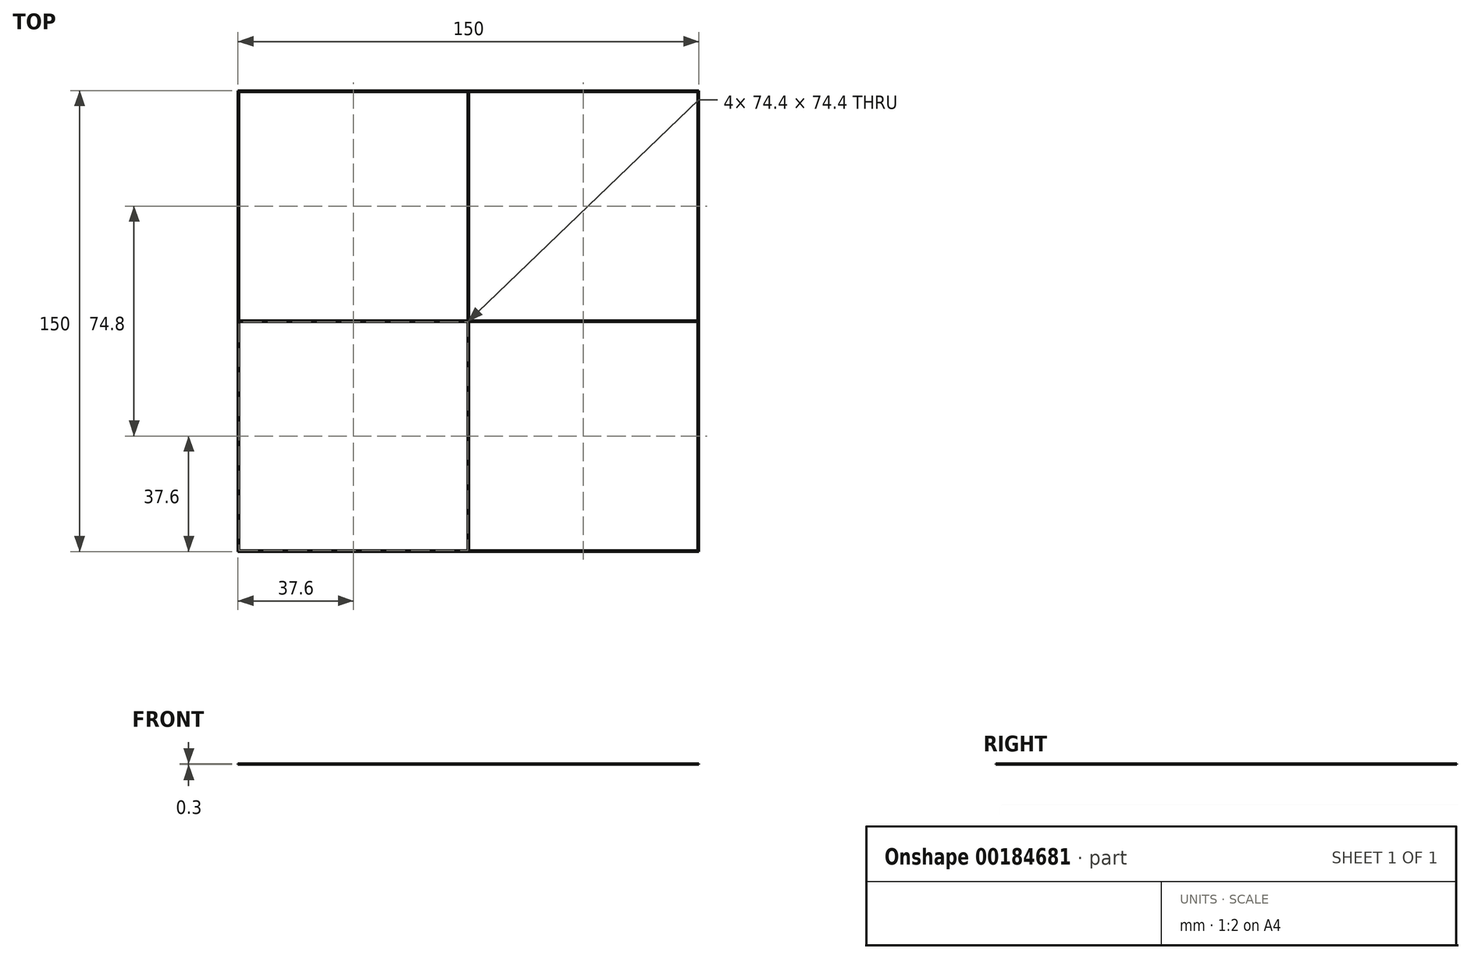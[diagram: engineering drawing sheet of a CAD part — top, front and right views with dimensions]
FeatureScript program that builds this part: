
annotation { "Feature Type Name" : "Feature", "Feature Type Description" : "" }
export const myFeature = defineFeature(function(context is Context, id is Id, definition is map)
    precondition{}
    {
        {
            var Q0;
            Q0=qCreatedBy(makeId("Top.planeOp"),FACE);
            var sketch = newSketch(context, id + "F0", { "sketchPlane" : qUnion([Q0])});
            skLineSegment(sketch, "E0.bottom", {"start": v(75, -75) * mm, "end": v(-75, -75) * mm});
            skLineSegment(sketch, "E0.top", {"start": v(75, 75) * mm, "end": v(-75, 75) * mm});
            skLineSegment(sketch, "E0.left", {"start": v(75, -75) * mm, "end": v(75, 75) * mm});
            skLineSegment(sketch, "E0.right", {"start": v(-75, -75) * mm, "end": v(-75, 75) * mm});
            skPoint(sketch, "E0.middle", {"position": v(0, 0) * mm});
            skLineSegment(sketch, "E1.bottom", {"start": v(74.6, 74.6) * mm, "end": v(0.2, 74.6) * mm});
            skLineSegment(sketch, "E1.top", {"start": v(74.6, 0.2) * mm, "end": v(0.2, 0.2) * mm});
            skLineSegment(sketch, "E1.left", {"start": v(74.6, 74.6) * mm, "end": v(74.6, 0.2) * mm});
            skLineSegment(sketch, "E1.right", {"start": v(0.2, 74.6) * mm, "end": v(0.2, 0.2) * mm});
            skLineSegment(sketch, "E2", {"start": v(-75, 0) * mm, "end": v(75, 0) * mm, "construction": true});
            skLineSegment(sketch, "E3", {"start": v(0, 75) * mm, "end": v(0, -75) * mm, "construction": true});
            skLineSegment(sketch, "E4.MirrorCS", {"start": v(-74.6, 74.6) * mm, "end": v(-74.6, 0.2) * mm});
            skLineSegment(sketch, "E5.MirrorCS", {"start": v(-74.6, 74.6) * mm, "end": v(-0.2, 74.6) * mm});
            skLineSegment(sketch, "E6.MirrorCS", {"start": v(-0.2, 74.6) * mm, "end": v(-0.2, 0.2) * mm});
            skLineSegment(sketch, "E7.MirrorCS", {"start": v(-74.6, 0.2) * mm, "end": v(-0.2, 0.2) * mm});
            skLineSegment(sketch, "E8.MirrorCS", {"start": v(-74.6, -0.2) * mm, "end": v(-0.2, -0.2) * mm});
            skLineSegment(sketch, "E9.MirrorCS", {"start": v(-0.2, -74.6) * mm, "end": v(-0.2, -0.2) * mm});
            skLineSegment(sketch, "E10.MirrorCS", {"start": v(0.2, -74.6) * mm, "end": v(0.2, -0.2) * mm});
            skLineSegment(sketch, "E11.MirrorCS", {"start": v(74.6, -0.2) * mm, "end": v(0.2, -0.2) * mm});
            skLineSegment(sketch, "E12.MirrorCS", {"start": v(74.6, -74.6) * mm, "end": v(74.6, -0.2) * mm});
            skLineSegment(sketch, "E13.MirrorCS", {"start": v(74.6, -74.6) * mm, "end": v(0.2, -74.6) * mm});
            skLineSegment(sketch, "E14.MirrorCS", {"start": v(-74.6, -74.6) * mm, "end": v(-0.2, -74.6) * mm});
            skLineSegment(sketch, "E15.MirrorCS", {"start": v(-74.6, -74.6) * mm, "end": v(-74.6, -0.2) * mm});
            skSolve(sketch);
        }
        {
            var Q0;
            Q0 = qSketchRegion(id + "F0", true);
            extrude(context, id + "F1", {"entities" : qUnion([Q0]), "depth" : .3 * mm});
        }
    });
